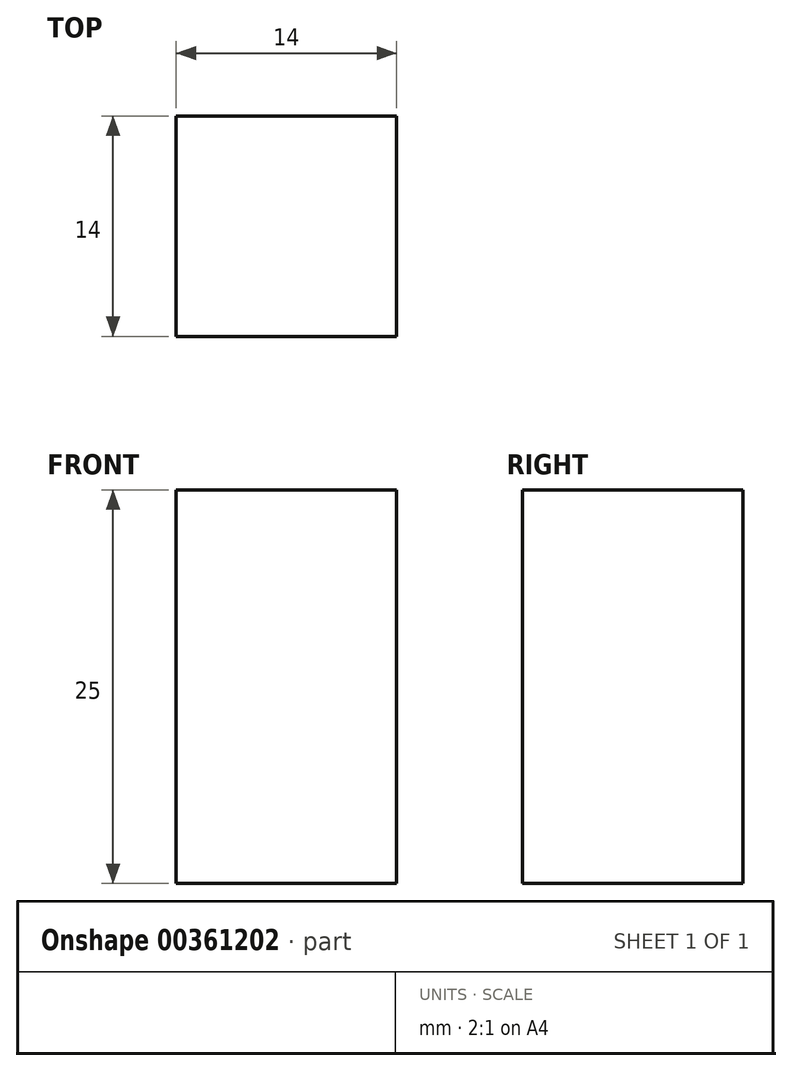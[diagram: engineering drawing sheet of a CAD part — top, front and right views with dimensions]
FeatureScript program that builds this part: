
annotation { "Feature Type Name" : "Feature", "Feature Type Description" : "" }
export const myFeature = defineFeature(function(context is Context, id is Id, definition is map)
    precondition{}
    {
        {
            var Q0;
            Q0=qCreatedBy(makeId("Top.planeOp"),FACE);
            var sketch = newSketch(context, id + "F0", { "sketchPlane" : qUnion([Q0])});
            skLineSegment(sketch, "E0.bottom", {"start": v(7, 7) * mm, "end": v(-7, 7) * mm});
            skLineSegment(sketch, "E0.top", {"start": v(7, -7) * mm, "end": v(-7, -7) * mm});
            skLineSegment(sketch, "E0.left", {"start": v(7, 7) * mm, "end": v(7, -7) * mm});
            skLineSegment(sketch, "E0.right", {"start": v(-7, 7) * mm, "end": v(-7, -7) * mm});
            skPoint(sketch, "E0.middle", {"position": v(0, 0) * mm});
            skSolve(sketch);
        }
        {
            var Q0;
            Q0 = qSketchRegion(id + "F0", true);
            extrude(context, id + "F1", {"entities" : qUnion([Q0]), "depth" : 25 * mm, "offsetDistance" : 25 * mm, "symmetric" : true});
        }
    });
